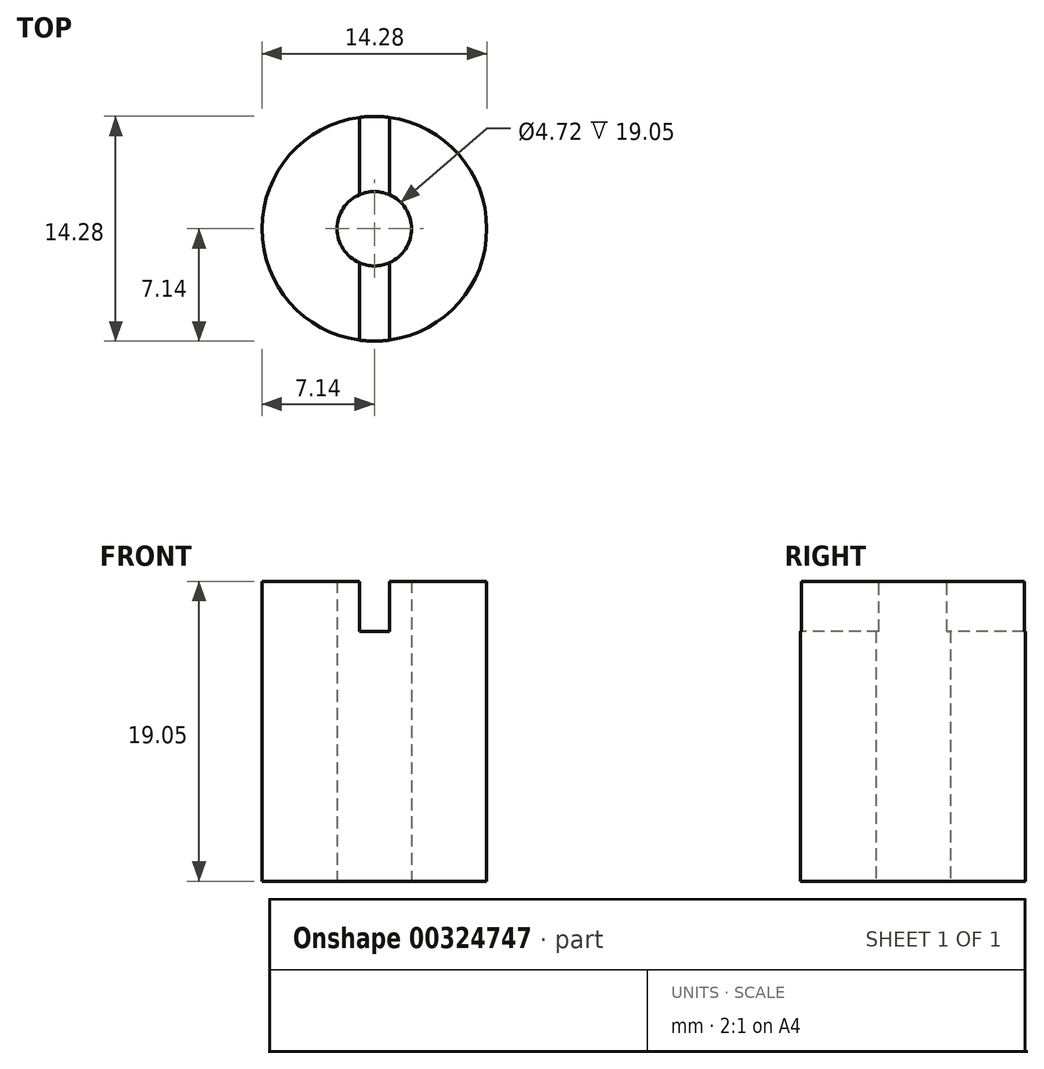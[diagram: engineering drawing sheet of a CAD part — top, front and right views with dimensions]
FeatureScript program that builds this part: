
annotation { "Feature Type Name" : "Feature", "Feature Type Description" : "" }
export const myFeature = defineFeature(function(context is Context, id is Id, definition is map)
    precondition{}
    {
        {
            var Q0;
            Q0=qCreatedBy(makeId("Top.planeOp"),FACE);
            var sketch = newSketch(context, id + "F0", { "sketchPlane" : qUnion([Q0])});
            skCircle(sketch, "E0", {"center": v(0, 0) * mm, "radius": 7.14 * mm});
            skCircle(sketch, "E1", {"center": v(0, 0) * mm, "radius": 2.36 * mm});
            skSolve(sketch);
        }
        {
            var Q0;
            Q0=makeQuery(id+"F0.imprint","IMPRINT",FACE,{"disambiguationData":[TD([[makeQuery(id+"F0.imprint","IMPRINT",EDGE,{"derivedFrom":sQuery(id+"F0.wireOp",EDGE,"E0")}),1.0]])]});
            extrude(context, id + "F1", {"entities" : qUnion([Q0]), "depth" : 19.05 * mm, "offsetDistance" : 25.4 * mm});
        }
        {
            var Q0;
            Q0=makeQuery(id+"F1.opExtrude","CAP_FACE",FACE,{"disambiguationData":[OSD([sQuery(id+"F0.wireOp",EDGE,"E0"),sQuery(id+"F0.wireOp",EDGE,"E1")])],"isStart":false});
            var sketch = newSketch(context, id + "F2", { "sketchPlane" : qUnion([Q0])});
            skLineSegment(sketch, "E2.bottom", {"start": v(-0.95, 7.62) * mm, "end": v(0.95, 7.62) * mm});
            skLineSegment(sketch, "E2.top", {"start": v(-0.95, -7.62) * mm, "end": v(0.95, -7.62) * mm});
            skLineSegment(sketch, "E2.left", {"start": v(-0.95, 7.62) * mm, "end": v(-0.95, -7.62) * mm});
            skLineSegment(sketch, "E2.right", {"start": v(0.95, 7.62) * mm, "end": v(0.95, -7.62) * mm});
            skPoint(sketch, "E2.middle", {"position": v(0, 0) * mm});
            skSolve(sketch);
        }
        {
            var Q0;
            {var subQ0=sQuery(id+"F2.wireOp",EDGE,"E2.left");var subQ1=makeQuery(id+"F1.opExtrude","CAP_EDGE",EDGE,{"disambiguationData":[OSD([sQuery(id+"F0.wireOp",EDGE,"E0")])],"isStart":false});var subQ2=makeQuery(id+"F2.imprint","INTERSECT",VERTEX,{"disambiguationData":[OD(0.0)],"derivedFrom":[subQ1,subQ0]});Q0=makeQuery(id+"F2.imprint","IMPRINT",FACE,{"disambiguationData":[TD([[makeQuery(id+"F2.imprint","IMPRINT",EDGE,{"disambiguationData":[TD([[subQ2,-1.0]])],"derivedFrom":subQ0}),1.0]])]});}
            var Q1;
            {var subQ0=sQuery(id+"F2.wireOp",EDGE,"E2.left");var subQ1=makeQuery(id+"F1.opExtrude","CAP_EDGE",EDGE,{"disambiguationData":[OSD([sQuery(id+"F0.wireOp",EDGE,"E0")])],"isStart":false});var subQ2=makeQuery(id+"F2.imprint","INTERSECT",VERTEX,{"disambiguationData":[OD(1.0)],"derivedFrom":[subQ1,subQ0]});Q1=makeQuery(id+"F2.imprint","IMPRINT",FACE,{"disambiguationData":[TD([[makeQuery(id+"F2.imprint","IMPRINT",EDGE,{"disambiguationData":[TD([[subQ2,1.0]])],"derivedFrom":subQ0}),1.0]])]});}
            extrude(context, id + "F3", {"entities" : qUnion([Q0, Q1]), "operationType" : NewBodyOperationType.REMOVE, "oppositeDirection" : true, "depth" : 3.17 * mm, "offsetDistance" : 25.4 * mm});
        }
    });
